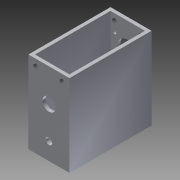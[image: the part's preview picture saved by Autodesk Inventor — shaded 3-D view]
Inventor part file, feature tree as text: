
AUTODESK INVENTOR PART (.ipt)
format: ipt  version: 2013 (Build 170138000, 138)  size: 163,328 bytes
history: native  units: mm
features: sketch x6, hole x4, thread x4, extrude x2, other x1
ambient origin geometry x1: Origin
feature tree (17):
  other  "ソリッド1"
  extrude  "押し出し1"  Depth=25.0mm
  extrude  "押し出し2"  Depth=50.0mm
  hole  "穴1"  [1 undecoded]
  hole  "穴2"  [1 undecoded]
  hole  "穴4"  [1 undecoded]
  thread  "ねじ1"
  thread  "ねじ2"
  thread  "ねじ3"
  thread  "ねじ4"
  hole  "穴5"  [1 undecoded]
  sketch  "スケッチ1"
  sketch  "スケッチ2"
  sketch  "スケッチ3"
  sketch  "スケッチ4"
  sketch  "スケッチ5"
  sketch  "スケッチ7"
note: 4 required parameter values undecoded (feature->parameter linkage not recoverable at this tier; creation-order binding heuristic only, values carry confidence <= 0.55)
